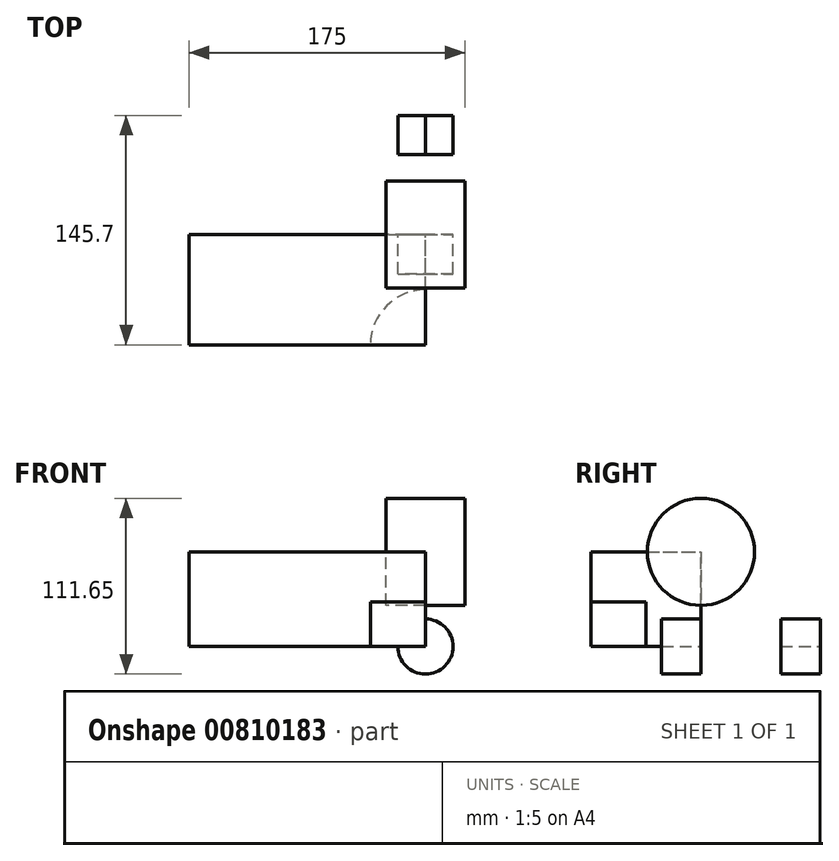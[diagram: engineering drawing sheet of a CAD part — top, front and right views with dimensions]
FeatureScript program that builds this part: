
annotation { "Feature Type Name" : "Feature", "Feature Type Description" : "" }
export const myFeature = defineFeature(function(context is Context, id is Id, definition is map)
    precondition{}
    {
        {
            var Q0;
            Q0=qCreatedBy(makeId("Front.planeOp"),FACE);
            var sketch = newSketch(context, id + "F0", { "sketchPlane" : qUnion([Q0])});
            skLineSegment(sketch, "E0.bottom", {"start": v(-75, 30.07) * mm, "end": v(75, 30.07) * mm});
            skLineSegment(sketch, "E0.top", {"start": v(-75, -30.07) * mm, "end": v(75, -30.07) * mm});
            skLineSegment(sketch, "E0.left", {"start": v(-75, 30.07) * mm, "end": v(-75, -30.07) * mm});
            skLineSegment(sketch, "E0.right", {"start": v(75, 30.07) * mm, "end": v(75, -30.07) * mm});
            skPoint(sketch, "E0.middle", {"position": v(0, 0) * mm});
            skSolve(sketch);
        }
        {
            var Q0;
            Q0 = qSketchRegion(id + "F0", true);
            extrude(context, id + "F1", {"entities" : qUnion([Q0]), "depth" : 70 * mm, "offsetDistance" : 25 * mm});
        }
        {
            var Q0;
            Q0=makeQuery(id+"F1.opExtrude","SWEPT_FACE",FACE,{"disambiguationData":[OSD([sQuery(id+"F0.wireOp",EDGE,"E0.top")])]});
            var sketch = newSketch(context, id + "F2", { "sketchPlane" : qUnion([Q0])});
            skCircle(sketch, "E1", {"center": v(75, 70) * mm, "radius": 35 * mm});
            skSolve(sketch);
        }
        {
            var Q0;
            Q0 = qSketchRegion(id + "F2", true);
            extrude(context, id + "F3", {"entities" : qUnion([Q0]), "operationType" : NewBodyOperationType.REMOVE, "oppositeDirection" : true, "depth" : 28.3 * mm, "offsetDistance" : 25 * mm});
        }
        {
            var Q0;
            Q0=makeQuery(id+"F1.opExtrude","CAP_FACE",FACE,{"disambiguationData":[OSD([sQuery(id+"F0.wireOp",EDGE,"E0.bottom"),sQuery(id+"F0.wireOp",EDGE,"E0.top"),sQuery(id+"F0.wireOp",EDGE,"E0.left"),sQuery(id+"F0.wireOp",EDGE,"E0.right")])],"isStart":true});
            var sketch = newSketch(context, id + "F4", { "sketchPlane" : qUnion([Q0])});
            skCircle(sketch, "E2", {"center": v(-75, -30.07) * mm, "radius": 17.5 * mm});
            skSolve(sketch);
        }
        {
            var Q0;
            {var subQ0=sQuery(id+"F4.wireOp",EDGE,"E2");var subQ1=makeQuery(id+"F1.opExtrude","CAP_EDGE",EDGE,{"disambiguationData":[OSD([sQuery(id+"F0.wireOp",EDGE,"E0.top")])],"isStart":true});var subQ2=makeQuery(id+"F4.imprint","INTERSECT",VERTEX,{"derivedFrom":[subQ1,subQ0]});Q0=makeQuery(id+"F4.imprint","IMPRINT",FACE,{"disambiguationData":[TD([[makeQuery(id+"F4.imprint","IMPRINT",EDGE,{"disambiguationData":[TD([[subQ2,1.0]])],"derivedFrom":subQ0}),1.0]])]});}
            extrude(context, id + "F5", {"entities" : qUnion([Q0]), "depth" : -25 * mm, "offsetDistance" : 25 * mm});
        }
        {
            var Q0;
            Q0=makeQuery(id+"F1.opExtrude","SWEPT_FACE",FACE,{"disambiguationData":[OSD([sQuery(id+"F0.wireOp",EDGE,"E0.right")])]});
            var sketch = newSketch(context, id + "F6", { "sketchPlane" : qUnion([Q0])});
            skCircle(sketch, "E3", {"center": v(0, 30.07) * mm, "radius": 34 * mm});
            skSolve(sketch);
        }
        {
            var Q0;
            Q0 = qSketchRegion(id + "F6", true);
            extrude(context, id + "F7", {"entities" : qUnion([Q0]), "operationType" : NewBodyOperationType.ADD, "depth" : 25 * mm, "offsetDistance" : 25 * mm, "hasSecondDirection" : true, "secondDirectionOppositeDirection" : true, "secondDirectionDepth" : 25 * mm});
        }
        {
            var Q0;
            Q0=makeQuery(id+"F5.opExtrude","SWEPT_BODY",BODY,{"disambiguationData":[OSD([sQuery(id+"F0.wireOp",EDGE,"E0.top"),sQuery(id+"F0.wireOp",EDGE,"E0.right"),sQuery(id+"F4.wireOp",EDGE,"E2")])]});
            transform(context, id + "F8", {"entities" : qUnion([Q0]), "transformType" : TransformType.TRANSLATION_3D, "dx" : 0 * mm, "dy" : 75.7 * mm, "dz" : 0 * mm, "makeCopy" : true});
        }
    });
